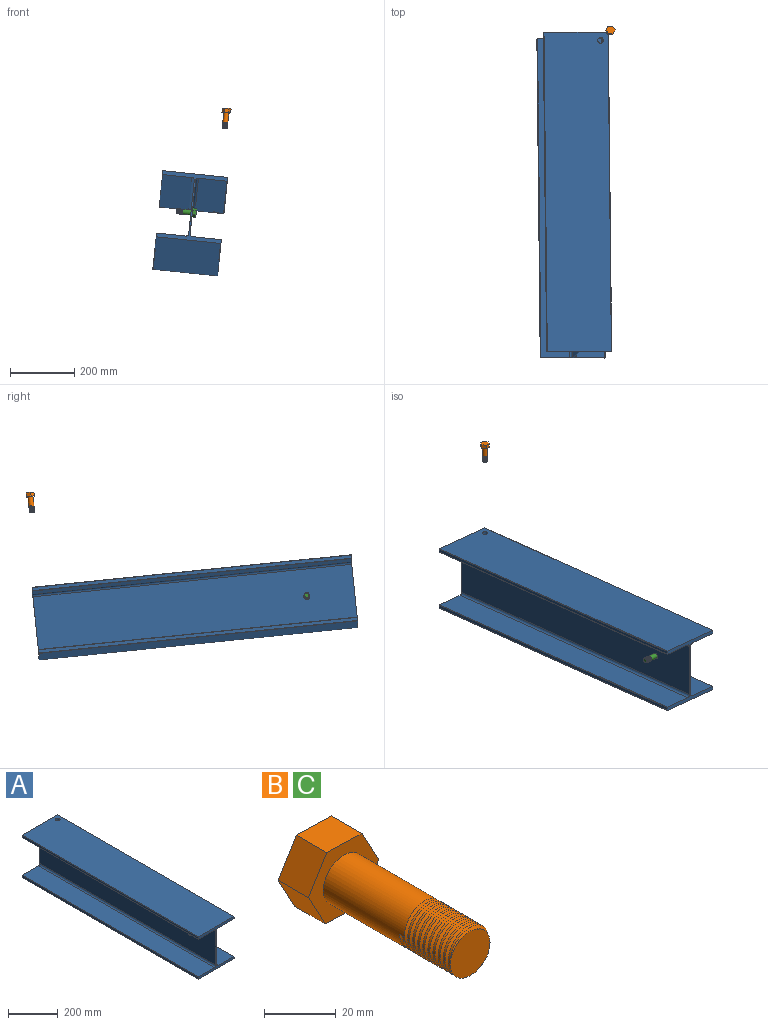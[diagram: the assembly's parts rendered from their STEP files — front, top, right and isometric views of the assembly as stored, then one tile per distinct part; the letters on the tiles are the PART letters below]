
ASSEMBLY  parts=3 mates=3
PART A: 28 faces, bbox 203x1000x208.4 mm
  f0: plane 1000x201mm, normal (0,0,1), area 200745.5mm2, adj f1,f23,f24,f25,f27
  f1: cylinder r=1mm len=1000mm, axis (0,1,0), area 1570.8mm2, adj f0,f2,f24,f25
  f2: plane 1000x10mm, normal (-1,0,0), area 10000mm2, adj f1,f3,f24,f25
  f3: cylinder r=1mm len=1000mm, axis (0,1,0), area 1570.8mm2, adj f2,f4,f24,f25
  f4: plane 1000x91.15mm, normal (0,0,-1), area 91150mm2, adj f3,f5,f24,f25
  f5: cylinder r=8mm len=1000mm, axis (0,1,0), area 12566.4mm2, adj f4,f6,f24,f25
  f6: plane 1000x168.35mm, normal (-1,0,0), area 168095.5mm2, adj f5,f7,f24,f25,f26
  f7: cylinder r=8mm len=1000mm, axis (0,1,0), area 12566.4mm2, adj f6,f8,f24,f25
  f8: plane 1000x91.15mm, normal (0,0,1), area 91150mm2, adj f7,f9,f24,f25
  f9: cylinder r=1mm len=1000mm, axis (0,1,0), area 1570.8mm2, adj f8,f10,f24,f25
  f10: plane 1000x10mm, normal (-1,0,0), area 10000mm2, adj f9,f11,f24,f25
  f11: cylinder r=1mm len=1000mm, axis (0,1,0), area 1570.8mm2, adj f10,f12,f24,f25
  f12: plane 1000x201mm, normal (0,0,-1), area 201000mm2, adj f11,f13,f24,f25
  f13: cylinder r=1mm len=1000mm, axis (0,1,0), area 1570.8mm2, adj f12,f14,f24,f25
  f14: plane 1000x10mm, normal (1,0,0), area 10000mm2, adj f13,f15,f24,f25
  f15: cylinder r=1mm len=1000mm, axis (0,1,0), area 1570.8mm2, adj f14,f16,f24,f25
  f16: plane 1000x89.5mm, normal (0,0,1), area 89500mm2, adj f15,f17,f24,f25
  f17: cylinder r=8mm len=1000mm, axis (0,1,0), area 12566.4mm2, adj f16,f18,f24,f25
  f18: plane 1000x168.35mm, normal (1,0,0), area 168095.5mm2, adj f17,f19,f24,f25,f26
  f19: cylinder r=8mm len=1000mm, axis (0,1,0), area 12566.4mm2, adj f18,f20,f24,f25
  f20: plane 1000x89.5mm, normal (0,0,-1), area 89245.5mm2, adj f19,f21,f24,f25,f27
  f21: cylinder r=1mm len=1000mm, axis (0,1,0), area 1570.8mm2, adj f20,f22,f24,f25
  f22: plane 1000x10mm, normal (1,0,0), area 10000mm2, adj f21,f23,f24,f25
  f23: cylinder r=1mm len=1000mm, axis (0,1,0), area 1570.8mm2, adj f0,f22,f24,f25
  f24: plane 208.35x203mm, normal (0,-1,0), area 5727.1mm2, adj f0,f1,f2,f3,f4,f5,f6,f7
  f25: plane 208.35x203mm, normal (0,1,0), area 5727.1mm2, adj f0,f1,f2,f3,f4,f5,f6,f7
  f26: cylinder r=9mm len=18mm, axis (1,0,0), area 246mm2, adj f6,f18
  f27: cylinder r=9mm len=18mm, axis (0,0,1), area 678.6mm2, adj f0,f20
PART B: 23 faces, bbox 28.2x63.4x24.9 mm
  f0: cylinder r=8mm len=32mm, axis (0,1,0), area 1558.2mm2, adj f1,f18,f20,f22
  f1: cylinder r=8mm len=16mm, axis (0,1,0), area 40.2mm2, adj f0,f2,f21,f22
  f2: cylinder r=8mm len=16mm, axis (0,1,0), area 40.2mm2, adj f1,f3,f21,f22
  f3: cylinder r=8mm len=16mm, axis (0,1,0), area 40.2mm2, adj f2,f4,f21,f22
  f4: cylinder r=8mm len=16mm, axis (0,1,0), area 40.2mm2, adj f3,f5,f21,f22
  f5: cylinder r=8mm len=16mm, axis (0,1,0), area 40.2mm2, adj f4,f6,f21,f22
  f6: cylinder r=8mm len=16mm, axis (0,1,0), area 40.2mm2, adj f5,f7,f21,f22
  f7: cylinder r=8mm len=16mm, axis (0,1,0), area 40.2mm2, adj f6,f8,f21,f22
  f8: cylinder r=8mm len=16mm, axis (0,1,0), area 40.2mm2, adj f7,f9,f21,f22
  f9: cylinder r=8mm len=16mm, axis (0,1,0), area 40.3mm2, adj f8,f10,f21,f22
  f10: cylinder r=8mm len=14.49mm, axis (0,1,0), area 8.1mm2, adj f9,f11,f21
  f11: plane 16.21x15.7mm, normal (0,-1,0), area 186.1mm2, adj f10,f21,f22
  f12: plane 13.85x12mm, normal (0.03,0,1), area 166.3mm2, adj f13,f17,f18,f19
  f13: plane 12x11.81mm, normal (-0.85,0,0.52), area 166.3mm2, adj f12,f14,f18,f19
  f14: plane 12.18x12mm, normal (-0.88,0,-0.48), area 166.3mm2, adj f13,f15,f18,f19
  f15: plane 13.85x12mm, normal (-0.03,0,-1), area 166.3mm2, adj f14,f16,f18,f19
  f16: plane 12x11.81mm, normal (0.85,0,-0.52), area 166.3mm2, adj f15,f17,f18,f19
  f17: plane 12.18x12mm, normal (0.88,0,0.48), area 166.3mm2, adj f12,f16,f18,f19
  f18: plane 27.7x24.36mm, normal (0,-1,0), area 297.8mm2, adj f0,f12,f13,f14,f15,f16,f17
  f19: plane 27.7x24.36mm, normal (0,1,0), area 498.8mm2, adj f12,f13,f14,f15,f16,f17
  f20: plane 1.2x1.04mm, normal (0,0,-1), area 0.6mm2, adj f0,f21,f22
  f21: bspline ~20.27x18.48mm, area 537.5mm2, adj f1,f2,f3,f4,f5,f6,f7,f8
  f22: bspline ~20.6x18.48mm, area 556.2mm2, adj f0,f1,f2,f3,f4,f5,f6,f7
PART C: same geometry as B
PLACE A rot(axis=(-0.71,0.71,0.04),8.3deg) t=(-291.65,451.43,-239.01)mm
PLACE B rot(axis=(1,0.06,-0.05),84.3deg) t=(-263.1,479.79,282.87)mm
PLACE C rot(axis=(-0.63,-0.58,-0.52),120deg) t=(-358.45,-383.74,-43.05)mm
MATE slider A.f26 <-> C.f0  axis (0.99,0,-0.1) through (-370.38,-383.74,-41.82)mm
MATE slider C.f0 <-> A.f26  axis (-0.99,0,0.1) through (-420.12,-383.74,-36.7)mm
MATE slider B.f0 <-> A.f27  axis (-0.1,-0.1,-0.99) through (-269.41,473.47,221.52)mm
